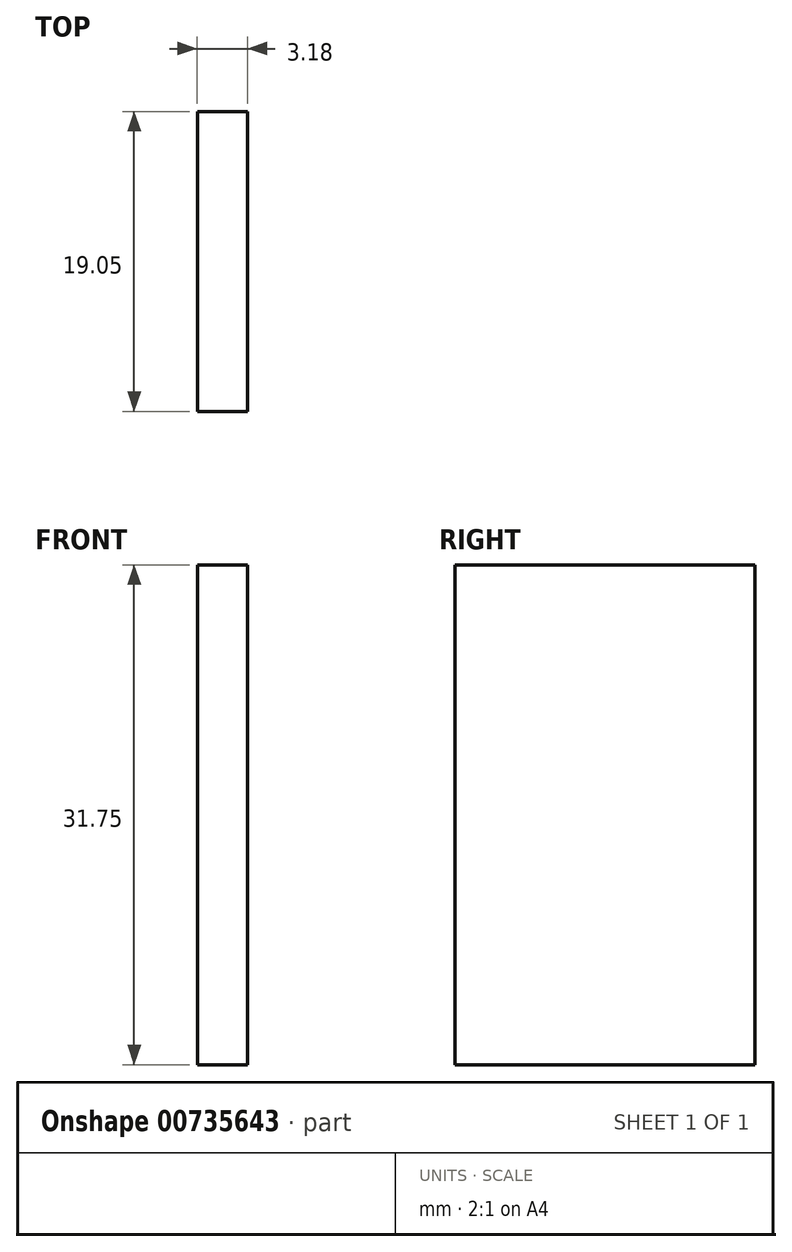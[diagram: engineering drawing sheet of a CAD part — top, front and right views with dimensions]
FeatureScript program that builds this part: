
annotation { "Feature Type Name" : "Feature", "Feature Type Description" : "" }
export const myFeature = defineFeature(function(context is Context, id is Id, definition is map)
    precondition{}
    {
        {
            var Q0;
            Q0=qCreatedBy(makeId("Top.planeOp"),FACE);
            var sketch = newSketch(context, id + "F0", { "sketchPlane" : qUnion([Q0])});
            skLineSegment(sketch, "E0.bottom", {"start": v(-39.5, 19.05) * mm, "end": v(-36.32, 19.05) * mm});
            skLineSegment(sketch, "E0.top", {"start": v(-39.5, 0) * mm, "end": v(-36.32, 0) * mm});
            skLineSegment(sketch, "E0.left", {"start": v(-39.5, 19.05) * mm, "end": v(-39.5, 0) * mm});
            skLineSegment(sketch, "E0.right", {"start": v(-36.32, 19.05) * mm, "end": v(-36.32, 0) * mm});
            skSolve(sketch);
        }
        {
            var Q0;
            Q0 = qSketchRegion(id + "F0", true);
            extrude(context, id + "F1", {"entities" : qUnion([Q0]), "depth" : 31.75 * mm, "offsetDistance" : 25.4 * mm});
        }
    });
